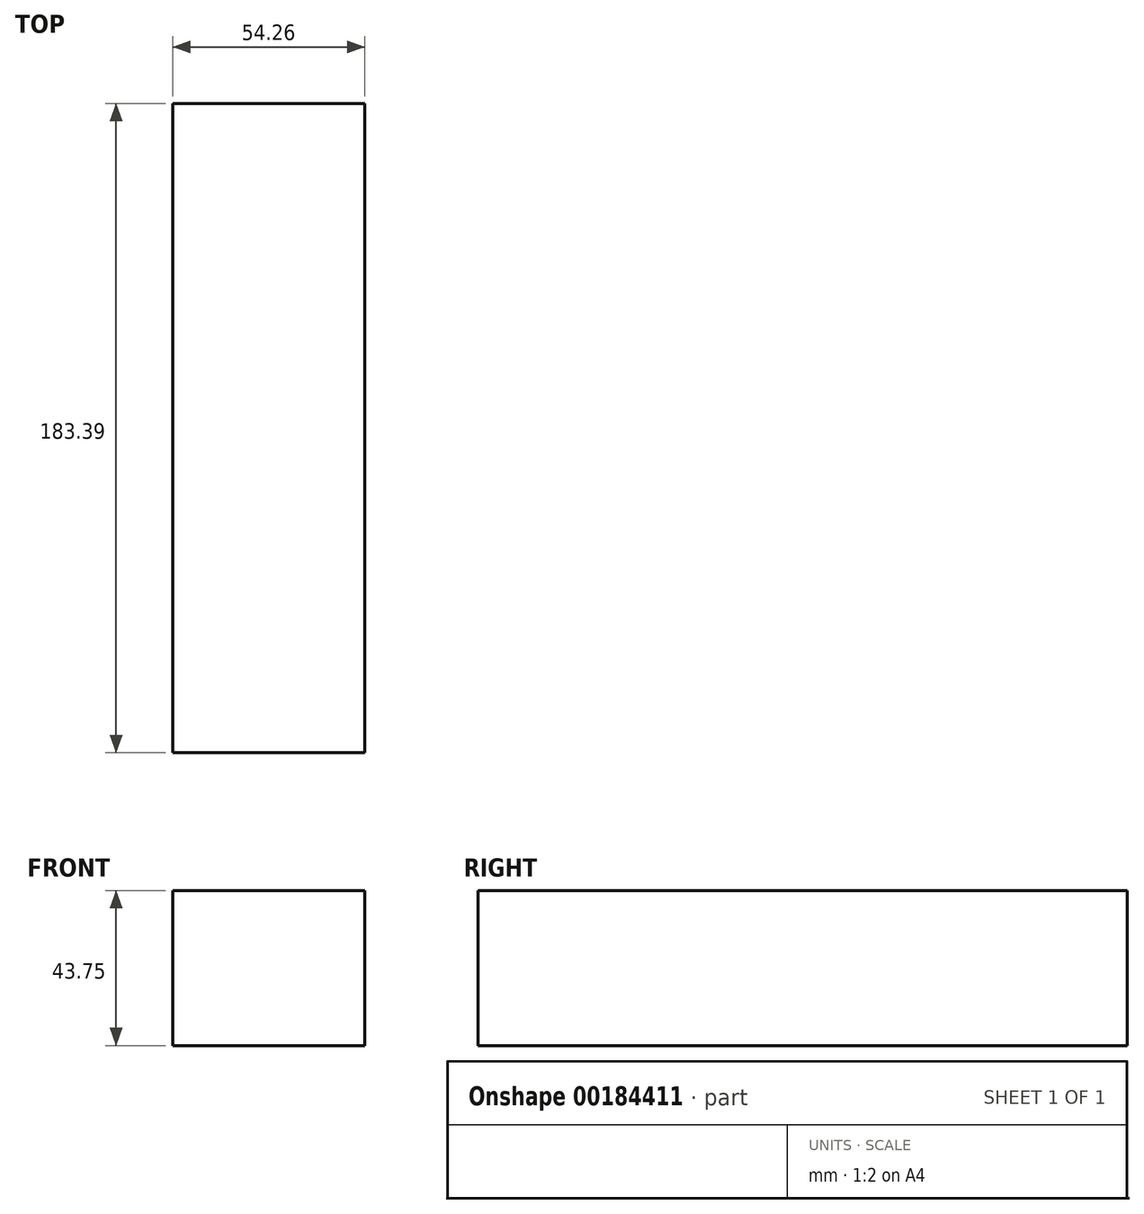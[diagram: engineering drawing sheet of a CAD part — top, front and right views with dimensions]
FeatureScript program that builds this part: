
annotation { "Feature Type Name" : "Feature", "Feature Type Description" : "" }
export const myFeature = defineFeature(function(context is Context, id is Id, definition is map)
    precondition{}
    {
        {
            var Q0;
            Q0=qCreatedBy(makeId("Front.planeOp"),FACE);
            var sketch = newSketch(context, id + "F0", { "sketchPlane" : qUnion([Q0])});
            skLineSegment(sketch, "E0.bottom", {"start": v(-25.79, 29.14) * mm, "end": v(28.47, 29.14) * mm});
            skLineSegment(sketch, "E0.top", {"start": v(-25.79, -14.61) * mm, "end": v(28.47, -14.61) * mm});
            skLineSegment(sketch, "E0.left", {"start": v(-25.79, 29.14) * mm, "end": v(-25.79, -14.61) * mm});
            skLineSegment(sketch, "E0.right", {"start": v(28.47, 29.14) * mm, "end": v(28.47, -14.61) * mm});
            skSolve(sketch);
        }
        {
            var Q0;
            Q0=makeQuery(id+"F0.imprint","IMPRINT",FACE,{"disambiguationData":[TD([[makeQuery(id+"F0.imprint","IMPRINT",EDGE,{"derivedFrom":sQuery(id+"F0.wireOp",EDGE,"E0.bottom")}),-1.0]])]});
            extrude(context, id + "F1", {"entities" : qUnion([Q0]), "depth" : 60.96 * mm});
        }
        {
            var Q0;
            Q0=makeQuery(id+"F1.opExtrude","CAP_FACE",FACE,{"disambiguationData":[OSD([sQuery(id+"F0.wireOp",EDGE,"E0.bottom"),sQuery(id+"F0.wireOp",EDGE,"E0.top"),sQuery(id+"F0.wireOp",EDGE,"E0.left"),sQuery(id+"F0.wireOp",EDGE,"E0.right")])],"isStart":false});
            extrude(context, id + "F2", {"entities" : qUnion([Q0]), "operationType" : NewBodyOperationType.ADD, "oppositeDirection" : true, "depth" : 40.4 * mm});
        }
        {
            var Q0;
            Q0=makeQuery(id+"F1.opExtrude","CAP_FACE",FACE,{"disambiguationData":[OSD([sQuery(id+"F0.wireOp",EDGE,"E0.bottom"),sQuery(id+"F0.wireOp",EDGE,"E0.top"),sQuery(id+"F0.wireOp",EDGE,"E0.left"),sQuery(id+"F0.wireOp",EDGE,"E0.right")])],"isStart":false});
            extrude(context, id + "F3", {"entities" : qUnion([Q0]), "operationType" : NewBodyOperationType.ADD, "depth" : 122.43 * mm});
        }
    });
